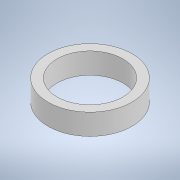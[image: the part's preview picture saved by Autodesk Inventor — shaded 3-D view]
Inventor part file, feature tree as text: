
AUTODESK INVENTOR PART (.ipt)
format: ipt  version: 2022 (Build 260153000, 153)  size: 102,912 bytes
history: native  units: in
note: dims shown in document units (in); Inventor stores cm internally (conversion verified against a paired STEP export)
features: extrude x1, sketch x1
ambient origin geometry x8: Origin, YZ Plane, XZ Plane, XY Plane, X Axis, Y Axis, Z Axis, Center Point
bodies: Solid1 (feature_tree)
feature tree (2):
  extrude  "Extrusion1"  Depth=0.0276in
  sketch  "Sketch1"  dims[d0=0.0866in d1=0.0118in d2=0.0276in d3=0.0in]
